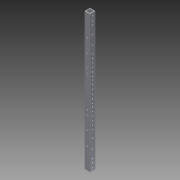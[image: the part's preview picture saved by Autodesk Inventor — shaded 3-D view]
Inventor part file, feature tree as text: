
AUTODESK INVENTOR PART (.ipt)
format: ipt  version: 2014 SP1 (Build 180222100, 222)  size: 233,984 bytes
history: native  units: in
note: dims shown in document units (in); Inventor stores cm internally (conversion verified against a paired STEP export)
features: reference x7, extrude x4, sketch x4
ambient origin geometry x8: Origin, YZ Plane, XZ Plane, XY Plane, X Axis, Y Axis, Z Axis, Center Point
bodies: Solid1 (feature_tree)
feature tree (15):
  extrude  "Extrusion1"  Depth=1.0in
  extrude  "Extrusion2"  Depth=26.0in TaperAngle=0.0deg
  extrude  "Extrusion3"  Depth=1.0in
  extrude  "Extrusion4"  Depth=0.75in
  sketch  "Sketch1"  dims[d0=1.0in d1=1.0in]
  sketch  "Sketch2"  dims[d2=0.125in d3=26.0in d4=0.0in]
  sketch  "Sketch3"  dims[d5=1.0in d6=0.0in d7=1.75in]
  reference  "Reference11"
  reference  "Reference12"
  reference  "Reference13"
  sketch  "Sketch4"  dims[d8=2.375in d9=1.75in d10=1.75in d11=0.26in d12=0.26in d13=0.26in d14=0.26in d15=0.26in d16=0.26in d17=0.26in d18=0.26in d19=1.0in d20=0.0in d21=2.375in d22=0.26in d23=0.26in d27=0.375in d28=0.375in d33=3.5in d34=0.26in d35=2.7559in d37=0.75in d38=0.3937in d40=1.0in d42=2.7559in d44=0.75in d45=0.3937in d47=1.0in d49=1.0in d50=0.0in d51=0.75in d52=0.75in d53=0.75in d54=0.75in]
  reference  "Reference15"
  reference  "Reference16"
  reference  "Reference17"
  reference  "Reference18"
